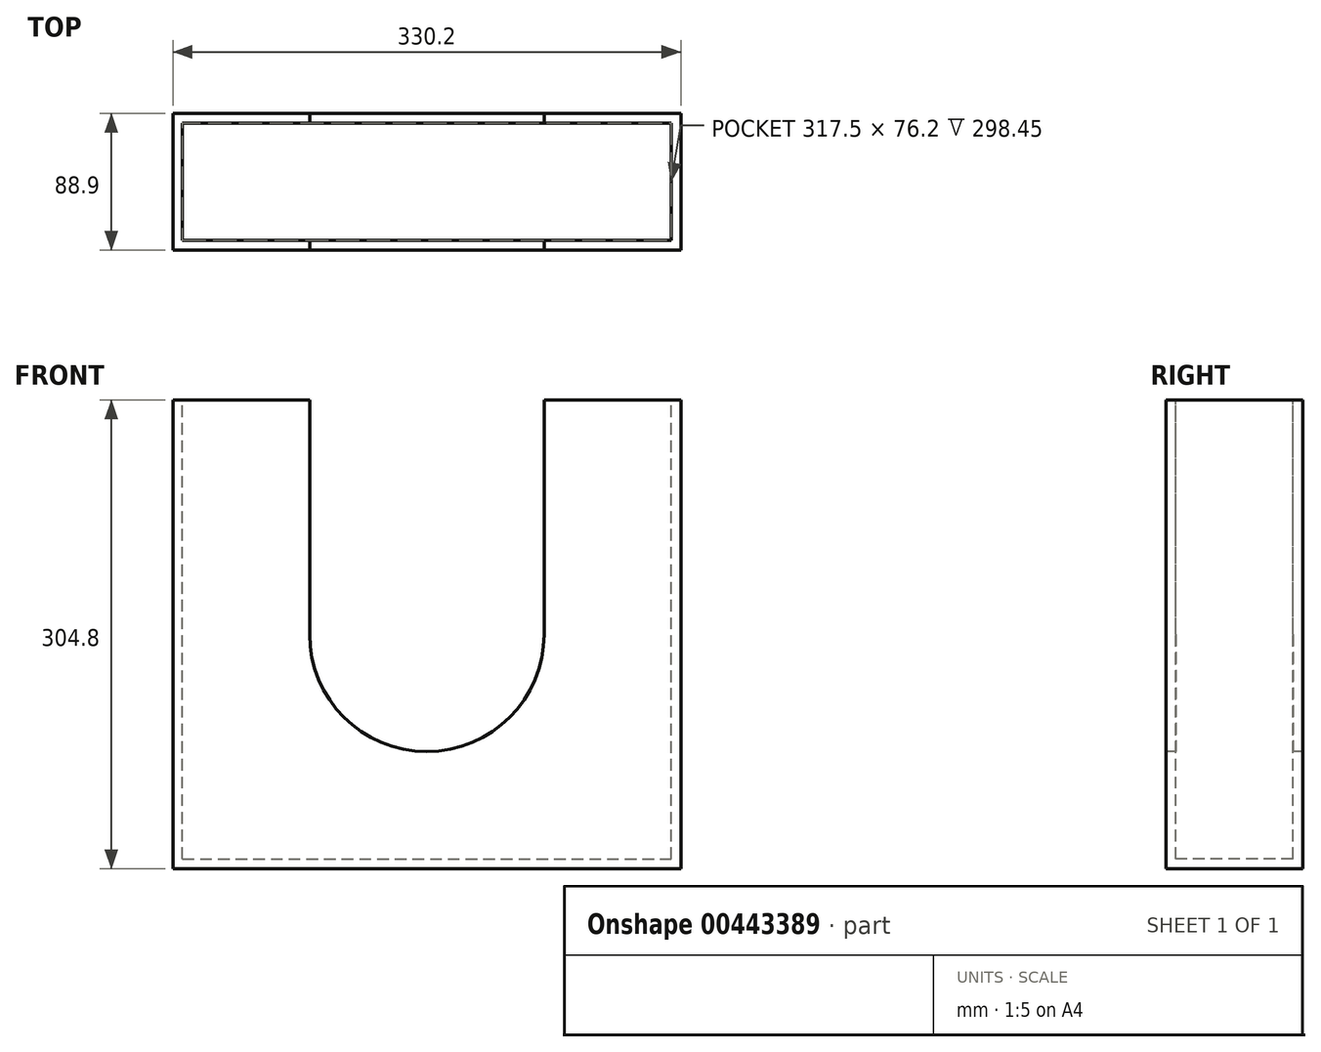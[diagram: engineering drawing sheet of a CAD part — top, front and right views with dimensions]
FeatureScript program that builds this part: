
annotation { "Feature Type Name" : "Feature", "Feature Type Description" : "" }
export const myFeature = defineFeature(function(context is Context, id is Id, definition is map)
    precondition{}
    {
        {
            var Q0;
            Q0=qCreatedBy(makeId("Front.planeOp"),FACE);
            var sketch = newSketch(context, id + "F0", { "sketchPlane" : qUnion([Q0])});
            skLineSegment(sketch, "E0.bottom", {"start": v(223.1, -16.14) * mm, "end": v(-107.1, -16.14) * mm});
            skLineSegment(sketch, "E0.top", {"start": v(223.1, 288.66) * mm, "end": v(-107.1, 288.66) * mm});
            skLineSegment(sketch, "E0.left", {"start": v(223.1, -16.14) * mm, "end": v(223.1, 288.66) * mm});
            skLineSegment(sketch, "E0.right", {"start": v(-107.1, -16.14) * mm, "end": v(-107.1, 288.66) * mm});
            skSolve(sketch);
        }
        {
            var Q0;
            Q0 = qSketchRegion(id + "F0", true);
            extrude(context, id + "F1", {"entities" : qUnion([Q0]), "depth" : 88.9 * mm});
        }
        {
            var Q0;
            Q0=makeQuery(id+"F1.opExtrude","SWEPT_FACE",FACE,{"disambiguationData":[OSD([sQuery(id+"F0.wireOp",EDGE,"E0.top")])]});
            var sketch = newSketch(context, id + "F2", { "sketchPlane" : qUnion([Q0])});
            skLineSegment(sketch, "E1.bottom", {"start": v(-100.74, -6.35) * mm, "end": v(216.76, -6.35) * mm});
            skLineSegment(sketch, "E1.top", {"start": v(-100.74, -82.55) * mm, "end": v(216.76, -82.55) * mm});
            skLineSegment(sketch, "E1.left", {"start": v(-100.74, -6.35) * mm, "end": v(-100.74, -82.55) * mm});
            skLineSegment(sketch, "E1.right", {"start": v(216.76, -6.35) * mm, "end": v(216.76, -82.55) * mm});
            skSolve(sketch);
        }
        {
            var Q0;
            Q0=makeQuery(id+"F2.imprint","IMPRINT",FACE,{"disambiguationData":[TD([[makeQuery(id+"F2.imprint","IMPRINT",EDGE,{"derivedFrom":sQuery(id+"F2.wireOp",EDGE,"E1.bottom")}),-1.0]])]});
            extrude(context, id + "F3", {"entities" : qUnion([Q0]), "operationType" : NewBodyOperationType.REMOVE, "oppositeDirection" : true, "depth" : 298.45 * mm});
        }
        {
            var Q0;
            Q0=makeQuery(id+"F1.opExtrude","CAP_FACE",FACE,{"disambiguationData":[OSD([sQuery(id+"F0.wireOp",EDGE,"E0.bottom"),sQuery(id+"F0.wireOp",EDGE,"E0.top"),sQuery(id+"F0.wireOp",EDGE,"E0.left"),sQuery(id+"F0.wireOp",EDGE,"E0.right")])],"isStart":false});
            var sketch = newSketch(context, id + "F4", { "sketchPlane" : qUnion([Q0])});
            skPoint(sketch, "E2.endSnap0", {"position": v(58, 288.66) * mm});
            skArc(sketch, "E3", {"start": v(-18.2, 136.26) * mm, "mid": v(58, 60.06) * mm, "end": v(134.2, 136.26) * mm});
            skLineSegment(sketch, "E4", {"start": v(-18.2, 136.26) * mm, "end": v(-18.2, 288.66) * mm});
            skLineSegment(sketch, "E5", {"start": v(134.2, 136.26) * mm, "end": v(134.2, 288.66) * mm});
            skSolve(sketch);
        }
        {
            var Q0;
            Q0=makeQuery(id+"F4.imprint","IMPRINT",FACE,{"disambiguationData":[TD([[makeQuery(id+"F4.imprint","IMPRINT",EDGE,{"derivedFrom":sQuery(id+"F4.wireOp",EDGE,"E3")}),1.0]])]});
            extrude(context, id + "F5", {"entities" : qUnion([Q0]), "operationType" : NewBodyOperationType.REMOVE, "oppositeDirection" : true, "depth" : 127 * mm});
        }
    });
